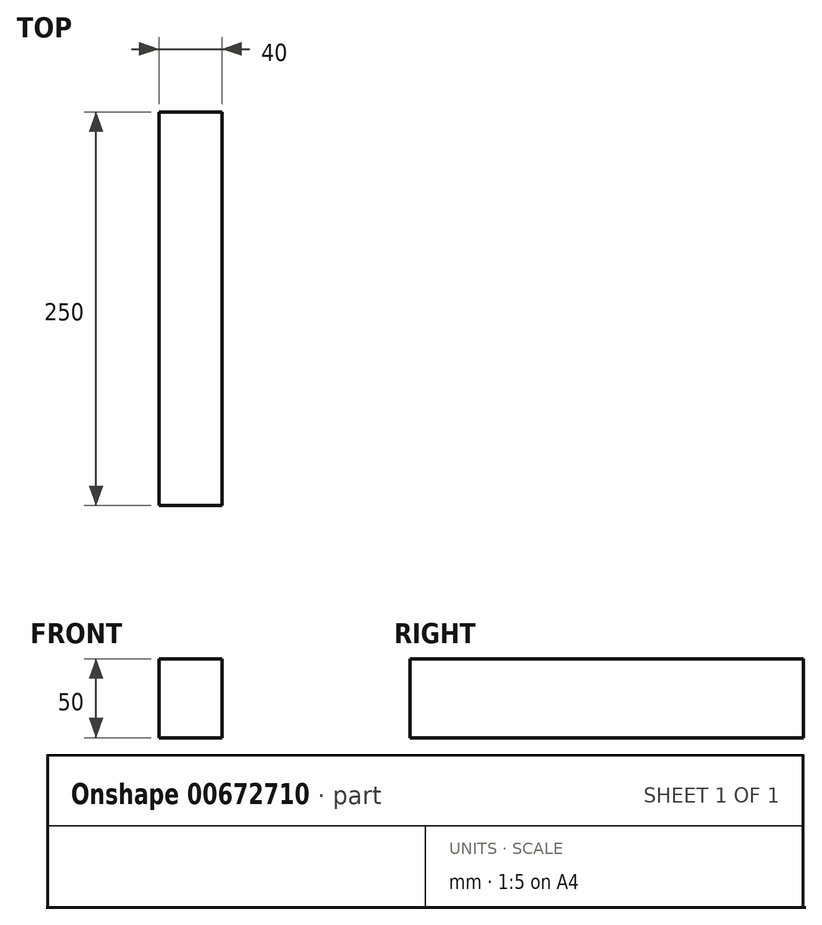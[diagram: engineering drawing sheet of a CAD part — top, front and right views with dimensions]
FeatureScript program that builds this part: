
annotation { "Feature Type Name" : "Feature", "Feature Type Description" : "" }
export const myFeature = defineFeature(function(context is Context, id is Id, definition is map)
    precondition{}
    {
        {
            var Q0;
            Q0=qCreatedBy(makeId("Front.planeOp"),FACE);
            var sketch = newSketch(context, id + "F0", { "sketchPlane" : qUnion([Q0])});
            skLineSegment(sketch, "E0.bottom", {"start": v(0, 0) * mm, "end": v(40, 0) * mm});
            skLineSegment(sketch, "E0.top", {"start": v(0, 50) * mm, "end": v(40, 50) * mm});
            skLineSegment(sketch, "E0.left", {"start": v(0, 0) * mm, "end": v(0, 50) * mm});
            skLineSegment(sketch, "E0.right", {"start": v(40, 0) * mm, "end": v(40, 50) * mm});
            skSolve(sketch);
        }
        {
            var Q0;
            Q0=makeQuery(id+"F0.imprint","IMPRINT",FACE,{"disambiguationData":[TD([[makeQuery(id+"F0.imprint","IMPRINT",EDGE,{"derivedFrom":sQuery(id+"F0.wireOp",EDGE,"E0.bottom")}),1.0]])]});
            extrude(context, id + "F1", {"entities" : qUnion([Q0]), "depth" : 250 * mm, "offsetDistance" : 25.4 * mm});
        }
    });
